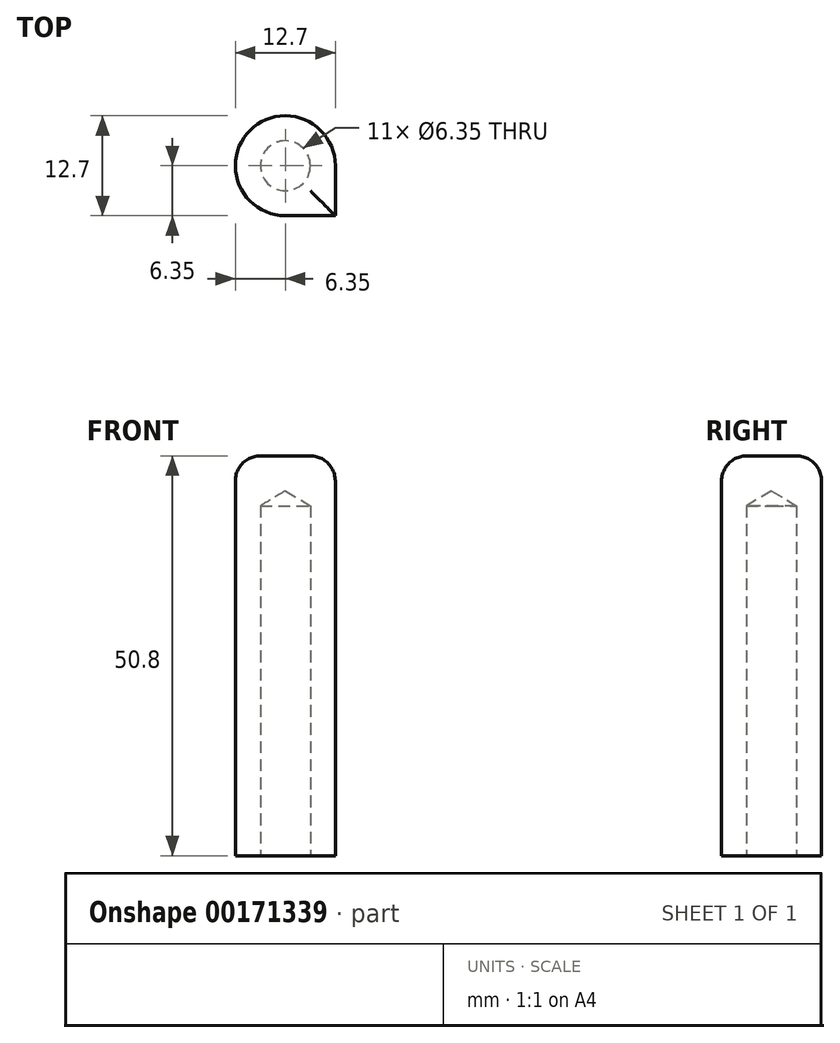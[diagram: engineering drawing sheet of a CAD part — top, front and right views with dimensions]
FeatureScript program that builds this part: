
annotation { "Feature Type Name" : "Feature", "Feature Type Description" : "" }
export const myFeature = defineFeature(function(context is Context, id is Id, definition is map)
    precondition{}
    {
        {
            var Q0;
            Q0=qCreatedBy(makeId("Top.planeOp"),FACE);
            var sketch = newSketch(context, id + "F0", { "sketchPlane" : qUnion([Q0])});
            skArc(sketch, "E0", {"start": v(6.35, 0) * mm, "mid": v(-4.5, 4.5) * mm, "end": v(0, -6.35) * mm});
            skLineSegment(sketch, "E1", {"start": v(0, -6.35) * mm, "end": v(6.35, -6.35) * mm});
            skLineSegment(sketch, "E2", {"start": v(6.35, -6.35) * mm, "end": v(6.35, 0) * mm});
            skSolve(sketch);
        }
        {
            var Q0;
            Q0=makeQuery(id+"F0.imprint","IMPRINT",FACE,{"disambiguationData":[TD([[makeQuery(id+"F0.imprint","IMPRINT",EDGE,{"derivedFrom":sQuery(id+"F0.wireOp",EDGE,"E0")}),1.0]])]});
            extrude(context, id + "F1", {"entities" : qUnion([Q0]), "depth" : 50.8 * mm});
        }
        {
            var Q0;
            Q0=makeQuery(id+"F1.opExtrude","CAP_FACE",FACE,{"disambiguationData":[OSD([sQuery(id+"F0.wireOp",EDGE,"E0"),sQuery(id+"F0.wireOp",EDGE,"E1"),sQuery(id+"F0.wireOp",EDGE,"E2")])],"isStart":false});
            fillet(context, id + "F2", {"entities" : qUnion([Q0]), "radius" : 3.17 * mm, "tangentPropagation" : true, "allowEdgeOverflow" : false});
        }
        {
            var Q0;
            Q0=sQuery(id+"F0.wireOp",VERTEX,"E0.center");
            var Q1;
            Q1=makeQuery(id+"F1.opExtrude","SWEPT_BODY",BODY,{"disambiguationData":[OSD([sQuery(id+"F0.wireOp",EDGE,"E0"),sQuery(id+"F0.wireOp",EDGE,"E1"),sQuery(id+"F0.wireOp",EDGE,"E2")])]});
            hole(context, id + "F3", {"style" : HoleStyle.SIMPLE, "endStyle" : HoleEndStyle.BLIND, "oppositeDirection" : true, "holeDiameter" : 6.35 * mm, "holeDepth" : 44.45 * mm, "locations" : qUnion([Q0]), "scope" : qUnion([Q1])});
        }
    });
